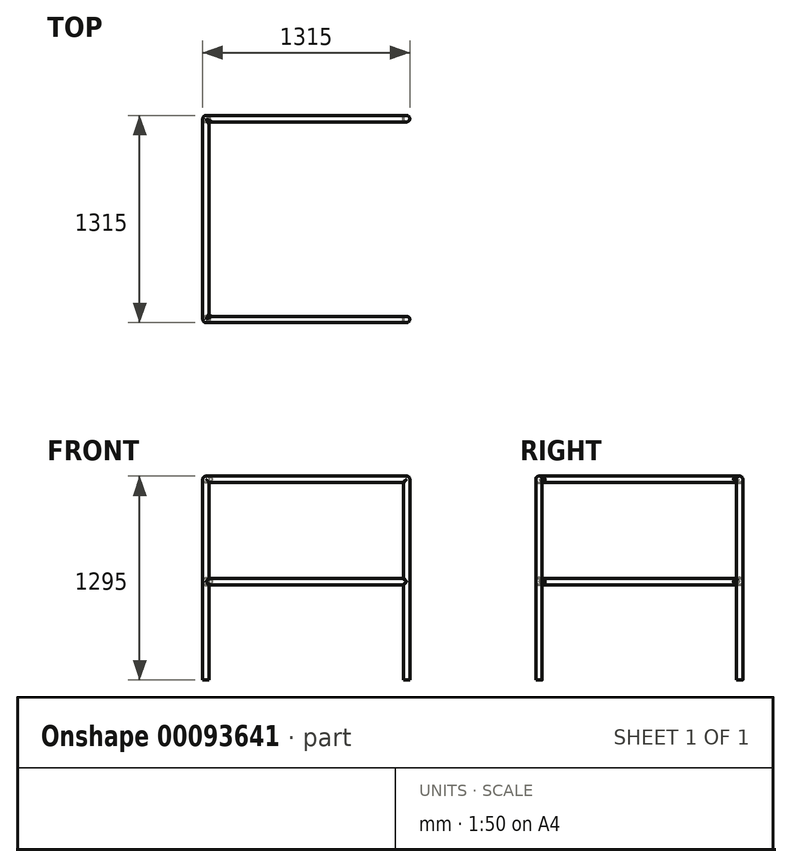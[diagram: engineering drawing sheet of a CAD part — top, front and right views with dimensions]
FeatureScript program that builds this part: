
annotation { "Feature Type Name" : "Feature", "Feature Type Description" : "" }
export const myFeature = defineFeature(function(context is Context, id is Id, definition is map)
    precondition{}
    {
        {
            var Q0;
            Q0=qCreatedBy(makeId("Top.planeOp"),FACE);
            var sketch = newSketch(context, id + "F0", { "sketchPlane" : qUnion([Q0])});
            skLineSegment(sketch, "E0.bottom", {"start": v(-637.5, -637.5) * mm, "end": v(637.5, -637.5) * mm});
            skLineSegment(sketch, "E0.top", {"start": v(-637.5, 637.5) * mm, "end": v(637.5, 637.5) * mm});
            skLineSegment(sketch, "E0.left", {"start": v(-637.5, -637.5) * mm, "end": v(-637.5, 637.5) * mm});
            skPoint(sketch, "E0.middle", {"position": v(0, 0) * mm});
            skPoint(sketch, "E1.visualSharp", {"position": v(-637.5, 637.5) * mm});
            skPoint(sketch, "E2.visualSharp", {"position": v(-637.5, -637.5) * mm});
            skSolve(sketch);
        }
        {
            var Q0;
            Q0=qCreatedBy(makeId("Right.planeOp"),FACE);
            cPlane(context, id + "F1", {"entities" : qUnion([Q0]), "cplaneType" : CPlaneType.OFFSET, "offset" : 637.5 * mm, "width" : 150 * mm, "height" : 150 * mm});
        }
        {
            var Q0;
            Q0=qCreatedBy(id+"F1.planeOp",FACE);
            var sketch = newSketch(context, id + "F2", { "sketchPlane" : qUnion([Q0])});
            skCircle(sketch, "E3", {"center": v(637.5, 0) * mm, "radius": 20 * mm});
            skCircle(sketch, "E4", {"center": v(637.5, -650) * mm, "radius": 20 * mm});
            skSolve(sketch);
        }
        {
            var Q0;
            Q0=makeQuery(id+"F2.imprint","IMPRINT",FACE,{"disambiguationData":[TD([[makeQuery(id+"F2.imprint","IMPRINT",EDGE,{"derivedFrom":sQuery(id+"F2.wireOp",EDGE,"E3")}),1.0]])]});
            var Q1;
            Q1=makeQuery(id+"F2.imprint","IMPRINT",FACE,{"disambiguationData":[TD([[makeQuery(id+"F2.imprint","IMPRINT",EDGE,{"derivedFrom":sQuery(id+"F2.wireOp",EDGE,"E4")}),1.0]])]});
            var Q2;
            Q2=sQuery(id+"F0.wireOp",EDGE,"E0.top");
            var Q3;
            Q3=sQuery(id+"F0.wireOp",EDGE,"E0.left");
            var Q4;
            Q4=sQuery(id+"F0.wireOp",EDGE,"E0.bottom");
            sweep(context, id + "F3", {"profiles" : qUnion([Q0, Q1]), "path" : qUnion([Q2, Q3, Q4])});
        }
        {
            var Q0;
            Q0=qCreatedBy(makeId("Top.planeOp"),FACE);
            var sketch = newSketch(context, id + "F4", { "sketchPlane" : qUnion([Q0])});
            skLineSegment(sketch, "E5.bottom", {"start": v(637.5, -637.5) * mm, "end": v(-637.5, -637.5) * mm, "construction": true});
            skLineSegment(sketch, "E5.top", {"start": v(637.5, 637.5) * mm, "end": v(-637.5, 637.5) * mm, "construction": true});
            skLineSegment(sketch, "E5.left", {"start": v(637.5, -637.5) * mm, "end": v(637.5, 637.5) * mm, "construction": true});
            skLineSegment(sketch, "E5.right", {"start": v(-637.5, -637.5) * mm, "end": v(-637.5, 637.5) * mm, "construction": true});
            skPoint(sketch, "E5.middle", {"position": v(0, 0) * mm});
            skCircle(sketch, "E6", {"center": v(-637.5, -637.5) * mm, "radius": 20 * mm});
            skCircle(sketch, "E7", {"center": v(637.5, -637.5) * mm, "radius": 20 * mm});
            skCircle(sketch, "E8", {"center": v(637.5, 637.5) * mm, "radius": 20 * mm});
            skCircle(sketch, "E9", {"center": v(-637.5, 637.5) * mm, "radius": 20 * mm});
            skSolve(sketch);
        }
        {
            var Q0;
            Q0=makeQuery(id+"F3.opSweep","MID_CAP_EDGE",EDGE,{"disambiguationData":[OSD([sQuery(id+"F0.wireOp",VERTEX,"E0.bottom.start"),sQuery(id+"F2.wireOp",EDGE,"E4")])],"capPos":2.0});
            var Q1;
            Q1=makeQuery(id+"F3.opSweep","MID_CAP_EDGE",EDGE,{"disambiguationData":[OSD([sQuery(id+"F0.wireOp",VERTEX,"E0.bottom.start"),sQuery(id+"F2.wireOp",EDGE,"E3")])],"capPos":2.0});
            var Q2;
            Q2=makeQuery(id+"F3.opSweep","MID_CAP_EDGE",EDGE,{"disambiguationData":[OSD([sQuery(id+"F0.wireOp",VERTEX,"E0.left.end"),sQuery(id+"F2.wireOp",EDGE,"E4")])],"capPos":1.0});
            var Q3;
            Q3=makeQuery(id+"F3.opSweep","MID_CAP_EDGE",EDGE,{"disambiguationData":[OSD([sQuery(id+"F0.wireOp",VERTEX,"E0.left.end"),sQuery(id+"F2.wireOp",EDGE,"E3")])],"capPos":1.0});
            fillet(context, id + "F5", {"entities" : qUnion([Q0, Q1, Q2, Q3]), "radius" : 20 * mm, "tangentPropagation" : true, "allowEdgeOverflow" : false});
        }
        {
            var Q0;
            Q0 = qSketchRegion(id + "F4", true);
            extrude(context, id + "F6", {"entities" : qUnion([Q0]), "operationType" : NewBodyOperationType.ADD, "oppositeDirection" : true, "depth" : 1275 * mm});
        }
        {
            var Q0;
            Q0=makeQuery(id+"F3.opSweep","CAP_FACE",FACE,{"disambiguationData":[OSD([sQuery(id+"F0.wireOp",VERTEX,"E0.bottom.end"),sQuery(id+"F2.wireOp",EDGE,"E3")])],"isStart":false});
            var Q1;
            Q1=makeQuery(id+"F3.opSweep","CAP_FACE",FACE,{"disambiguationData":[OSD([sQuery(id+"F0.wireOp",VERTEX,"E0.top.end"),sQuery(id+"F2.wireOp",EDGE,"E3")])],"isStart":true});
            var Q2;
            Q2=makeQuery(id+"F6.boolean.opBoolean","INTERSECT",EDGE,{"derivedFrom":[makeQuery(id+"F3.opSweep","CAP_FACE",FACE,{"disambiguationData":[OSD([sQuery(id+"F0.wireOp",VERTEX,"E0.bottom.end"),sQuery(id+"F2.wireOp",EDGE,"E3")])],"isStart":false}),makeQuery(id+"F6.opExtrude","CAP_FACE",FACE,{"disambiguationData":[OSD([sQuery(id+"F4.wireOp",EDGE,"E7")])],"isStart":true})]});
            revolve(context, id + "F7", {"operationType" : NewBodyOperationType.ADD, "entities" : qUnion([Q0, Q1]), "axis" : qUnion([Q2]), "revolveType" : RevolveType.FULL});
        }
        {
            var Q0;
            Q0=makeQuery(id+"F6.boolean.opBoolean","INTERSECT",EDGE,{"disambiguationData":[OD(1.0)],"derivedFrom":[makeQuery(id+"F3.opSweep","SWEPT_FACE",FACE,{"disambiguationData":[OSD([sQuery(id+"F0.wireOp",EDGE,"E0.left"),sQuery(id+"F2.wireOp",EDGE,"E4")])]}),makeQuery(id+"F6.opExtrude","SWEPT_FACE",FACE,{"disambiguationData":[OSD([sQuery(id+"F4.wireOp",EDGE,"E9")])]})]});
            var Q1;
            Q1=makeQuery(id+"F6.boolean.opBoolean","INTERSECT",EDGE,{"disambiguationData":[OD(0.0)],"derivedFrom":[makeQuery(id+"F5.opFillet","BLEND_FACE",FACE,{"disambiguationData":[OSD([sQuery(id+"F0.wireOp",VERTEX,"E0.left.end"),sQuery(id+"F2.wireOp",EDGE,"E4")]),OD(0.0)]}),makeQuery(id+"F6.opExtrude","SWEPT_FACE",FACE,{"disambiguationData":[OSD([sQuery(id+"F4.wireOp",EDGE,"E9")])]})]});
            var Q2;
            Q2=makeQuery(id+"F6.boolean.opBoolean","INTERSECT",EDGE,{"disambiguationData":[OD(1.0)],"derivedFrom":[makeQuery(id+"F3.opSweep","SWEPT_FACE",FACE,{"disambiguationData":[OSD([sQuery(id+"F0.wireOp",EDGE,"E0.bottom"),sQuery(id+"F2.wireOp",EDGE,"E4")])]}),makeQuery(id+"F6.opExtrude","SWEPT_FACE",FACE,{"disambiguationData":[OSD([sQuery(id+"F4.wireOp",EDGE,"E6")])]})]});
            var Q3;
            Q3=makeQuery(id+"F6.boolean.opBoolean","INTERSECT",EDGE,{"disambiguationData":[OD(0.0)],"derivedFrom":[makeQuery(id+"F3.opSweep","SWEPT_FACE",FACE,{"disambiguationData":[OSD([sQuery(id+"F0.wireOp",EDGE,"E0.bottom"),sQuery(id+"F2.wireOp",EDGE,"E4")])]}),makeQuery(id+"F6.opExtrude","SWEPT_FACE",FACE,{"disambiguationData":[OSD([sQuery(id+"F4.wireOp",EDGE,"E6")])]})]});
            var Q4;
            Q4=makeQuery(id+"F6.boolean.opBoolean","INTERSECT",EDGE,{"disambiguationData":[OD(0.0)],"derivedFrom":[makeQuery(id+"F3.opSweep","SWEPT_FACE",FACE,{"disambiguationData":[OSD([sQuery(id+"F0.wireOp",EDGE,"E0.bottom"),sQuery(id+"F2.wireOp",EDGE,"E4")])]}),makeQuery(id+"F6.opExtrude","SWEPT_FACE",FACE,{"disambiguationData":[OSD([sQuery(id+"F4.wireOp",EDGE,"E7")])]})]});
            var Q5;
            Q5=makeQuery(id+"F6.boolean.opBoolean","INTERSECT",EDGE,{"disambiguationData":[OD(1.0)],"derivedFrom":[makeQuery(id+"F3.opSweep","SWEPT_FACE",FACE,{"disambiguationData":[OSD([sQuery(id+"F0.wireOp",EDGE,"E0.top"),sQuery(id+"F2.wireOp",EDGE,"E4")])]}),makeQuery(id+"F6.opExtrude","SWEPT_FACE",FACE,{"disambiguationData":[OSD([sQuery(id+"F4.wireOp",EDGE,"E8")])]})]});
            var Q6;
            Q6=makeQuery(id+"F6.boolean.opBoolean","INTERSECT",EDGE,{"disambiguationData":[OD(0.0)],"derivedFrom":[makeQuery(id+"F3.opSweep","SWEPT_FACE",FACE,{"disambiguationData":[OSD([sQuery(id+"F0.wireOp",EDGE,"E0.top"),sQuery(id+"F2.wireOp",EDGE,"E4")])]}),makeQuery(id+"F6.opExtrude","SWEPT_FACE",FACE,{"disambiguationData":[OSD([sQuery(id+"F4.wireOp",EDGE,"E8")])]})]});
            var Q7;
            Q7=makeQuery(id+"F6.boolean.opBoolean","INTERSECT",EDGE,{"disambiguationData":[OD(1.0)],"derivedFrom":[makeQuery(id+"F3.opSweep","SWEPT_FACE",FACE,{"disambiguationData":[OSD([sQuery(id+"F0.wireOp",EDGE,"E0.bottom"),sQuery(id+"F2.wireOp",EDGE,"E4")])]}),makeQuery(id+"F6.opExtrude","SWEPT_FACE",FACE,{"disambiguationData":[OSD([sQuery(id+"F4.wireOp",EDGE,"E7")])]})]});
            var Q8;
            Q8=makeQuery(id+"F6.boolean.opBoolean","INTERSECT",EDGE,{"derivedFrom":[makeQuery(id+"F3.opSweep","SWEPT_FACE",FACE,{"disambiguationData":[OSD([sQuery(id+"F0.wireOp",EDGE,"E0.bottom"),sQuery(id+"F2.wireOp",EDGE,"E3")])]}),makeQuery(id+"F6.opExtrude","SWEPT_FACE",FACE,{"disambiguationData":[OSD([sQuery(id+"F4.wireOp",EDGE,"E7")])]})]});
            var Q9;
            Q9=makeQuery(id+"F6.boolean.opBoolean","INTERSECT",EDGE,{"derivedFrom":[makeQuery(id+"F3.opSweep","SWEPT_FACE",FACE,{"disambiguationData":[OSD([sQuery(id+"F0.wireOp",EDGE,"E0.top"),sQuery(id+"F2.wireOp",EDGE,"E3")])]}),makeQuery(id+"F6.opExtrude","SWEPT_FACE",FACE,{"disambiguationData":[OSD([sQuery(id+"F4.wireOp",EDGE,"E8")])]})]});
            fillet(context, id + "F8", {"entities" : qUnion([Q0, Q1, Q2, Q3, Q4, Q5, Q6, Q7, Q8, Q9]), "radius" : 5 * mm, "tangentPropagation" : true, "allowEdgeOverflow" : false});
        }
    });
